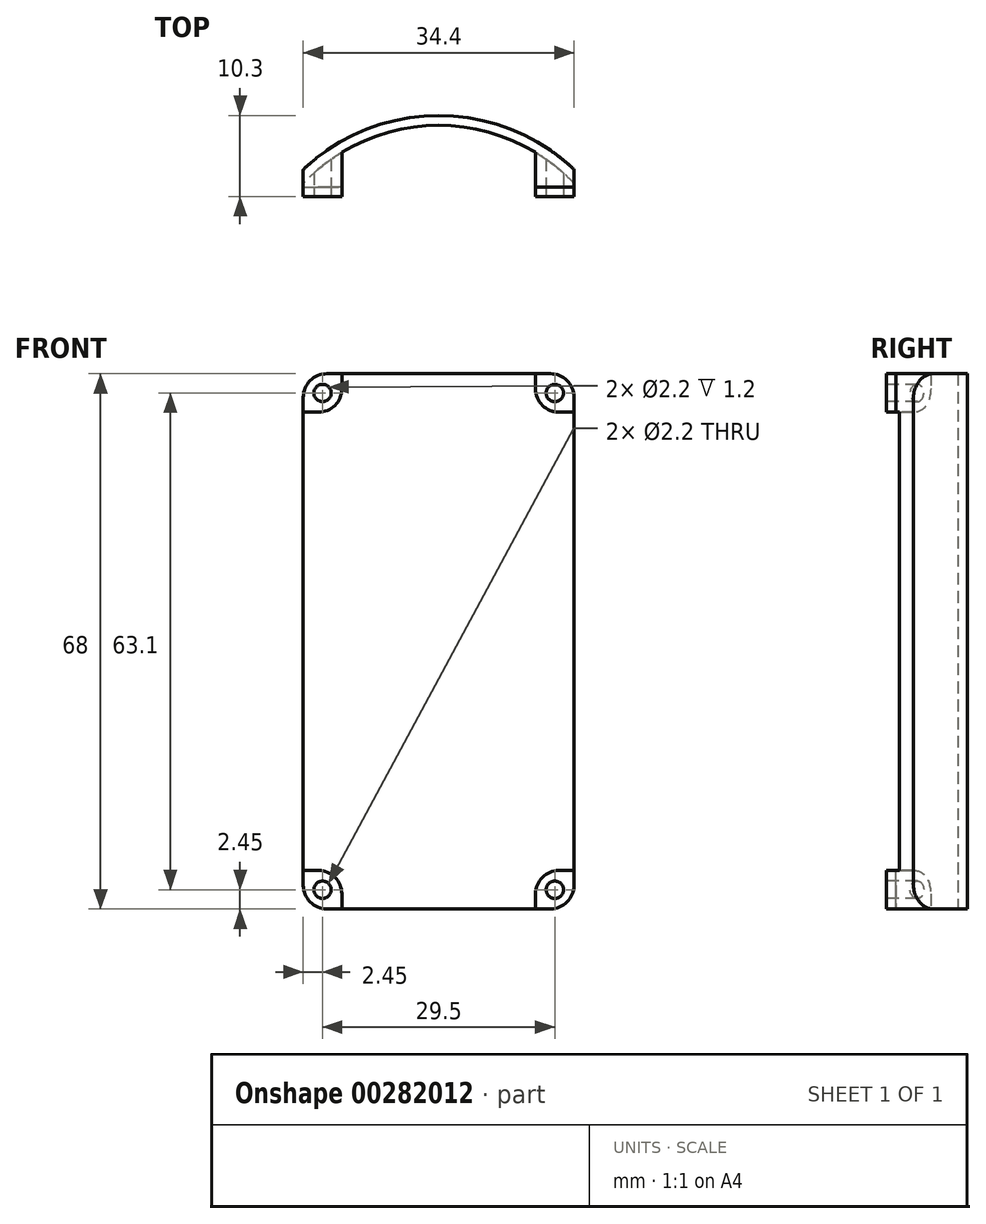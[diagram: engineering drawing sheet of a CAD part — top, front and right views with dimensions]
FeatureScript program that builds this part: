
annotation { "Feature Type Name" : "Feature", "Feature Type Description" : "" }
export const myFeature = defineFeature(function(context is Context, id is Id, definition is map)
    precondition{}
    {
        {
            var Q0;
            Q0=qCreatedBy(makeId("Top.planeOp"),FACE);
            var sketch = newSketch(context, id + "F0", { "sketchPlane" : qUnion([Q0])});
            skArc(sketch, "E0", {"start": v(17.2, 3.44) * mm, "mid": v(0, 10.3) * mm, "end": v(-17.2, 3.44) * mm});
            skArc(sketch, "E1", {"start": v(17.2, 1.68) * mm, "mid": v(0, 9.05) * mm, "end": v(-17.2, 1.68) * mm});
            skLineSegment(sketch, "E2", {"start": v(-17.2, 3.44) * mm, "end": v(-17.2, 1.68) * mm});
            skLineSegment(sketch, "E3", {"start": v(17.2, 3.44) * mm, "end": v(17.2, 1.68) * mm});
            skSolve(sketch);
        }
        {
            var Q0;
            Q0=makeQuery(id+"F0.imprint","IMPRINT",FACE,{"disambiguationData":[TD([[makeQuery(id+"F0.imprint","IMPRINT",EDGE,{"derivedFrom":sQuery(id+"F0.wireOp",EDGE,"E0")}),1.0]])]});
            extrude(context, id + "F1", {"entities" : qUnion([Q0]), "endBound" : BoundingType.SYMMETRIC, "depth" : 68 * mm});
        }
        {
            var Q0;
            Q0=qCreatedBy(makeId("Front.planeOp"),FACE);
            var sketch = newSketch(context, id + "F2", { "sketchPlane" : qUnion([Q0])});
            skLineSegment(sketch, "E4.bottom", {"start": v(-17.2, 34) * mm, "end": v(-12.3, 34) * mm});
            skLineSegment(sketch, "E4.top", {"start": v(-17.2, 29.1) * mm, "end": v(-15.3, 29.1) * mm});
            skLineSegment(sketch, "E4.left", {"start": v(-17.2, 34) * mm, "end": v(-17.2, 29.1) * mm});
            skLineSegment(sketch, "E4.right", {"start": v(-12.3, 34) * mm, "end": v(-12.3, 32.1) * mm});
            skCircle(sketch, "E5", {"center": v(-14.75, 31.55) * mm, "radius": 1.1 * mm});
            skPoint(sketch, "E5.centerSnap0", {"position": v(-17.2, 31.55) * mm});
            skPoint(sketch, "E5.centerSnap1", {"position": v(-14.75, 34) * mm});
            skPoint(sketch, "E6.visualSharp", {"position": v(-12.3, 29.1) * mm});
            skArc(sketch, "E6.filletArc", {"start": v(-15.3, 29.1) * mm, "mid": v(-13.18, 29.98) * mm, "end": v(-12.3, 32.1) * mm});
            skLineSegment(sketch, "E7", {"start": v(0, 0) * mm, "end": v(0, 50.45) * mm, "construction": true});
            skLineSegment(sketch, "E8", {"start": v(0, 0) * mm, "end": v(-28.2, 0) * mm, "construction": true});
            skLineSegment(sketch, "E9.MirrorCS", {"start": v(-17.2, -29.1) * mm, "end": v(-15.3, -29.1) * mm});
            skLineSegment(sketch, "E10.MirrorCS", {"start": v(-17.2, -34) * mm, "end": v(-17.2, -29.1) * mm});
            skLineSegment(sketch, "E11.MirrorCS", {"start": v(-12.3, -34) * mm, "end": v(-12.3, -32.1) * mm});
            skArc(sketch, "E12.MirrorCS", {"start": v(-15.3, -29.1) * mm, "mid": v(-13.18, -29.98) * mm, "end": v(-12.3, -32.1) * mm});
            skCircle(sketch, "E13.MirrorC", {"center": v(-14.75, -31.55) * mm, "radius": 1.1 * mm});
            skLineSegment(sketch, "E14.MirrorCS", {"start": v(17.2, 29.1) * mm, "end": v(15.3, 29.1) * mm});
            skLineSegment(sketch, "E15.MirrorCS", {"start": v(17.2, 34) * mm, "end": v(17.2, 29.1) * mm});
            skArc(sketch, "E16.MirrorCS", {"start": v(15.3, 29.1) * mm, "mid": v(13.18, 29.98) * mm, "end": v(12.3, 32.1) * mm});
            skCircle(sketch, "E17.MirrorC", {"center": v(14.75, 31.55) * mm, "radius": 1.1 * mm});
            skLineSegment(sketch, "E18.MirrorCS", {"start": v(12.3, 34) * mm, "end": v(12.3, 32.1) * mm});
            skLineSegment(sketch, "E19.MirrorCS", {"start": v(17.2, 34) * mm, "end": v(12.3, 34) * mm});
            skLineSegment(sketch, "E20.MirrorCS", {"start": v(17.2, -34) * mm, "end": v(17.2, -29.1) * mm});
            skCircle(sketch, "E21.MirrorC", {"center": v(14.75, -31.55) * mm, "radius": 1.1 * mm});
            skArc(sketch, "E22.MirrorCS", {"start": v(15.3, -29.1) * mm, "mid": v(13.18, -29.98) * mm, "end": v(12.3, -32.1) * mm});
            skLineSegment(sketch, "E23.MirrorCS", {"start": v(17.2, -29.1) * mm, "end": v(15.3, -29.1) * mm});
            skLineSegment(sketch, "E24.MirrorCS", {"start": v(12.3, -34) * mm, "end": v(12.3, -32.1) * mm});
            skLineSegment(sketch, "E25", {"start": v(-17.2, -34) * mm, "end": v(-12.3, -34) * mm});
            skLineSegment(sketch, "E26", {"start": v(12.3, -34) * mm, "end": v(17.2, -34) * mm});
            skSolve(sketch);
        }
        {
            var Q0;
            Q0=makeQuery(id+"F2.imprint","IMPRINT",FACE,{"disambiguationData":[TD([[makeQuery(id+"F2.imprint","IMPRINT",EDGE,{"derivedFrom":sQuery(id+"F2.wireOp",EDGE,"E14.MirrorCS")}),-1.0]])]});
            var Q1;
            Q1=makeQuery(id+"F2.imprint","IMPRINT",FACE,{"disambiguationData":[TD([[makeQuery(id+"F2.imprint","IMPRINT",EDGE,{"derivedFrom":sQuery(id+"F2.wireOp",EDGE,"E4.bottom")}),-1.0]])]});
            var Q2;
            Q2=makeQuery(id+"F2.imprint","IMPRINT",FACE,{"disambiguationData":[TD([[makeQuery(id+"F2.imprint","IMPRINT",EDGE,{"derivedFrom":sQuery(id+"F2.wireOp",EDGE,"E17.MirrorC")}),-1.0]])]});
            var Q3;
            Q3=makeQuery(id+"F2.imprint","IMPRINT",FACE,{"disambiguationData":[TD([[makeQuery(id+"F2.imprint","IMPRINT",EDGE,{"derivedFrom":sQuery(id+"F2.wireOp",EDGE,"E5")}),1.0]])]});
            var Q4;
            Q4=makeQuery(id+"F2.imprint","IMPRINT",FACE,{"disambiguationData":[TD([[makeQuery(id+"F2.imprint","IMPRINT",EDGE,{"derivedFrom":sQuery(id+"F2.wireOp",EDGE,"E9.MirrorCS")}),-1.0]])]});
            var Q5;
            Q5=makeQuery(id+"F2.imprint","IMPRINT",FACE,{"disambiguationData":[TD([[makeQuery(id+"F2.imprint","IMPRINT",EDGE,{"derivedFrom":sQuery(id+"F2.wireOp",EDGE,"E13.MirrorC")}),-1.0]])]});
            var Q6;
            Q6=makeQuery(id+"F2.imprint","IMPRINT",FACE,{"disambiguationData":[TD([[makeQuery(id+"F2.imprint","IMPRINT",EDGE,{"derivedFrom":sQuery(id+"F2.wireOp",EDGE,"E20.MirrorCS")}),1.0]])]});
            var Q7;
            Q7=makeQuery(id+"F2.imprint","IMPRINT",FACE,{"disambiguationData":[TD([[makeQuery(id+"F2.imprint","IMPRINT",EDGE,{"derivedFrom":sQuery(id+"F2.wireOp",EDGE,"E21.MirrorC")}),1.0]])]});
            var Q8;
            Q8=makeQuery(id+"F1.opExtrude","SWEPT_BODY",BODY,{"disambiguationData":[OSD([sQuery(id+"F0.wireOp",EDGE,"E0"),sQuery(id+"F0.wireOp",EDGE,"E1"),sQuery(id+"F0.wireOp",EDGE,"E2"),sQuery(id+"F0.wireOp",EDGE,"E3")])]});
            extrude(context, id + "F3", {"entities" : qUnion([Q0, Q1, Q2, Q3, Q4, Q5, Q6, Q7]), "operationType" : NewBodyOperationType.ADD, "endBound" : BoundingType.UP_TO_BODY, "oppositeDirection" : true, "endBoundEntityBody" : qUnion([Q8]), "depth" : 25 * mm});
        }
        {
            var Q0;
            Q0=makeQuery(id+"F2.imprint","IMPRINT",FACE,{"disambiguationData":[TD([[makeQuery(id+"F2.imprint","IMPRINT",EDGE,{"derivedFrom":sQuery(id+"F2.wireOp",EDGE,"E13.MirrorC")}),-1.0]])]});
            var Q1;
            Q1=makeQuery(id+"F2.imprint","IMPRINT",FACE,{"disambiguationData":[TD([[makeQuery(id+"F2.imprint","IMPRINT",EDGE,{"derivedFrom":sQuery(id+"F2.wireOp",EDGE,"E5")}),1.0]])]});
            var Q2;
            Q2=makeQuery(id+"F2.imprint","IMPRINT",FACE,{"disambiguationData":[TD([[makeQuery(id+"F2.imprint","IMPRINT",EDGE,{"derivedFrom":sQuery(id+"F2.wireOp",EDGE,"E17.MirrorC")}),-1.0]])]});
            var Q3;
            Q3=makeQuery(id+"F2.imprint","IMPRINT",FACE,{"disambiguationData":[TD([[makeQuery(id+"F2.imprint","IMPRINT",EDGE,{"derivedFrom":sQuery(id+"F2.wireOp",EDGE,"E21.MirrorC")}),1.0]])]});
            extrude(context, id + "F4", {"entities" : qUnion([Q0, Q1, Q2, Q3]), "operationType" : NewBodyOperationType.REMOVE, "oppositeDirection" : true, "depth" : 1.2 * mm});
        }
        {
            var Q0;
            {var subQ0=sQuery(id+"F0.wireOp",EDGE,"E2");var subQ1=sQuery(id+"F0.wireOp",EDGE,"E1");Q0=makeQuery(id+"F3.boolean.opBoolean","MERGE",EDGE,{"derivedFrom":[makeQuery(id+"F1.opExtrude","CAP_EDGE",EDGE,{"disambiguationData":[OSD([subQ0])],"isStart":false}),makeQuery(id+"F3.opExtrude","SWEPT_EDGE",EDGE,{"disambiguationData":[OSD([subQ1,subQ0]),TDD([makeQuery(id+"F1.opExtrude","CAP_VERTEX",VERTEX,{"disambiguationData":[OSD([subQ1,subQ0])],"isStart":false})])]})]});}
            var Q1;
            Q1=makeQuery(id+"F3.boolean.opBoolean","MERGE",EDGE,{"derivedFrom":[makeQuery(id+"F1.opExtrude","CAP_EDGE",EDGE,{"disambiguationData":[OSD([sQuery(id+"F0.wireOp",EDGE,"E3")])],"isStart":false}),makeQuery(id+"F3.opExtrude","SWEPT_EDGE",EDGE,{"disambiguationData":[OSD([sQuery(id+"F2.wireOp",EDGE,"E15.MirrorCS"),sQuery(id+"F2.wireOp",EDGE,"E19.MirrorCS")])]})]});
            var Q2;
            {var subQ0=sQuery(id+"F0.wireOp",EDGE,"E2");var subQ1=sQuery(id+"F0.wireOp",EDGE,"E1");Q2=makeQuery(id+"F3.boolean.opBoolean","MERGE",EDGE,{"derivedFrom":[makeQuery(id+"F1.opExtrude","CAP_EDGE",EDGE,{"disambiguationData":[OSD([subQ0])],"isStart":true}),makeQuery(id+"F3.opExtrude","SWEPT_EDGE",EDGE,{"disambiguationData":[OSD([subQ1,subQ0]),TDD([makeQuery(id+"F1.opExtrude","CAP_VERTEX",VERTEX,{"disambiguationData":[OSD([subQ1,subQ0])],"isStart":true})])]})]});}
            var Q3;
            Q3=makeQuery(id+"F3.boolean.opBoolean","MERGE",EDGE,{"derivedFrom":[makeQuery(id+"F1.opExtrude","CAP_EDGE",EDGE,{"disambiguationData":[OSD([sQuery(id+"F0.wireOp",EDGE,"E3")])],"isStart":true}),makeQuery(id+"F3.opExtrude","SWEPT_EDGE",EDGE,{"disambiguationData":[OSD([sQuery(id+"F2.wireOp",EDGE,"E20.MirrorCS"),sQuery(id+"F2.wireOp",EDGE,"E26")])]})]});
            fillet(context, id + "F5", {"entities" : qUnion([Q0, Q1, Q2, Q3]), "radius" : 3 * mm, "tangentPropagation" : true, "allowEdgeOverflow" : false});
        }
    });
